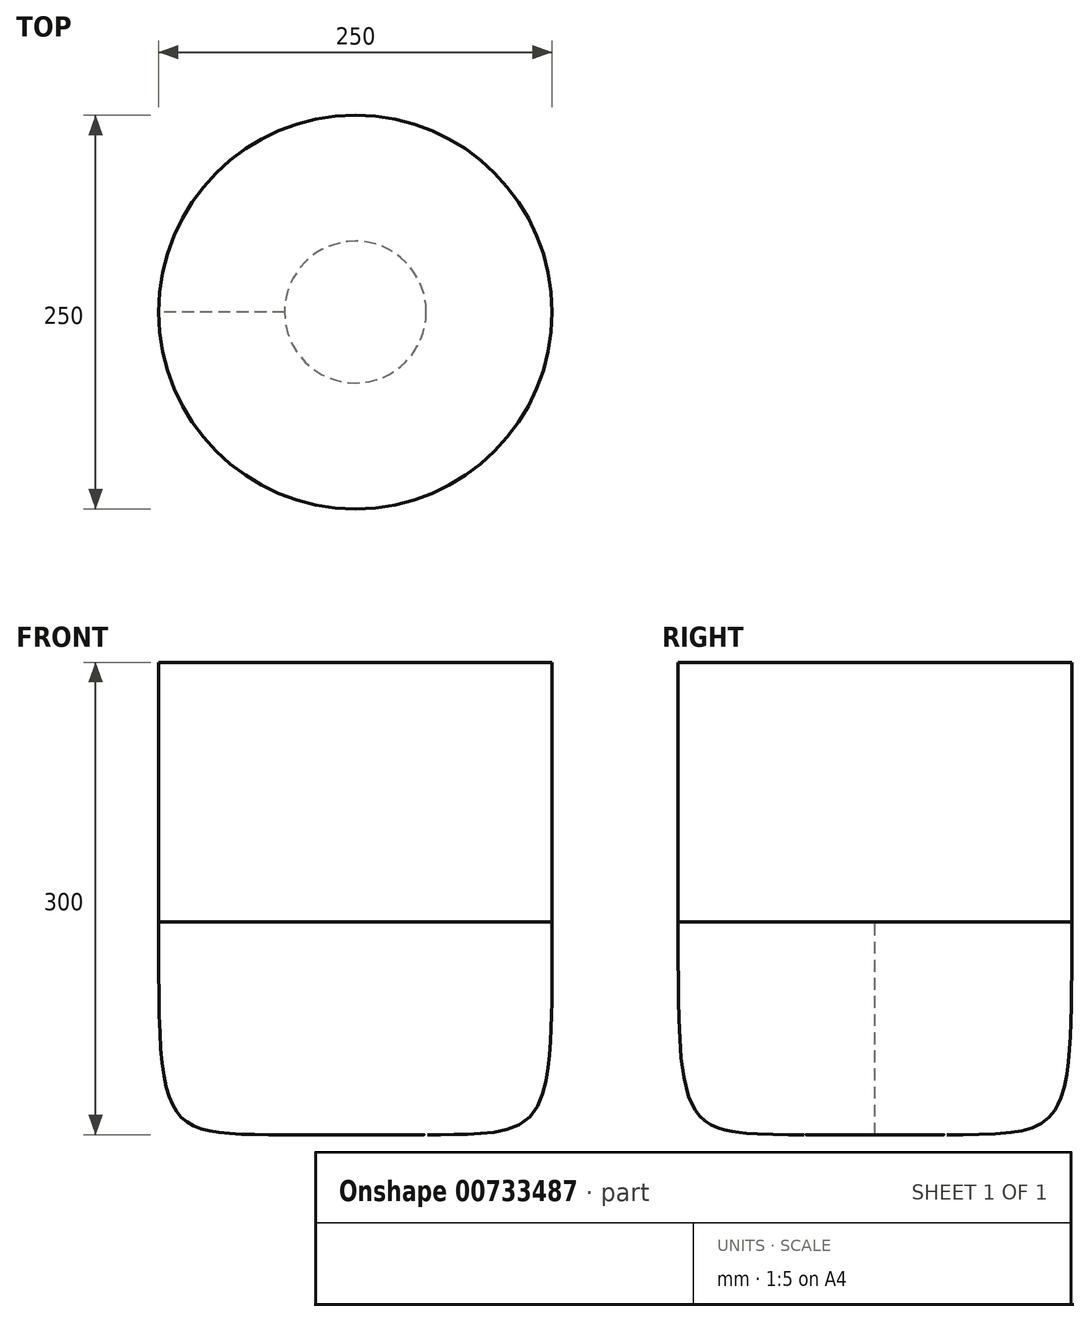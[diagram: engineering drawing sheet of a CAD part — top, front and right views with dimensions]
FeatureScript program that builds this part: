
annotation { "Feature Type Name" : "Feature", "Feature Type Description" : "" }
export const myFeature = defineFeature(function(context is Context, id is Id, definition is map)
    precondition{}
    {
        {
            var Q0;
            Q0=qCreatedBy(makeId("Front.planeOp"),FACE);
            var sketch = newSketch(context, id + "F0", { "sketchPlane" : qUnion([Q0])});
            skLineSegment(sketch, "E0.bottom", {"start": v(125, 150) * mm, "end": v(-125, 150) * mm});
            skLineSegment(sketch, "E0.top", {"start": v(125, -150) * mm, "end": v(-125, -150) * mm});
            skLineSegment(sketch, "E0.left", {"start": v(125, 150) * mm, "end": v(125, -150) * mm});
            skLineSegment(sketch, "E0.right", {"start": v(-125, 150) * mm, "end": v(-125, -150) * mm});
            skPoint(sketch, "E1", {"position": v(0, -150) * mm});
            skPoint(sketch, "E2", {"position": v(-125, 0) * mm});
            skPoint(sketch, "E3", {"position": v(125, 0) * mm});
            skPoint(sketch, "E4", {"position": v(45, -150) * mm});
            skPoint(sketch, "E5", {"position": v(-45, -150) * mm});
            skPoint(sketch, "E6", {"position": v(-125, -15) * mm});
            skPoint(sketch, "E7", {"position": v(-125, 15) * mm});
            skPoint(sketch, "E8", {"position": v(125, -15) * mm});
            skPoint(sketch, "E9", {"position": v(125, 15) * mm});
            skLineSegment(sketch, "E10", {"start": v(0, -150) * mm, "end": v(0, 150) * mm});
            skFitSpline(sketch, "E11", {"points": [v(-45, -150) * mm, v(-125, -15) * mm], "startDerivative": vector(-240, 0) * mm, "endDerivative": vector(0, 405) * mm});
            skFitSpline(sketch, "E12", {"points": [v(45, -150) * mm, v(125, -15) * mm], "startDerivative": vector(240, 0) * mm, "endDerivative": vector(0, 405) * mm});
            skLineSegment(sketch, "E13.bottom", {"start": v(-125, 15) * mm, "end": v(-125, 15) * mm});
            skLineSegment(sketch, "E13.top", {"start": v(-125, -15) * mm, "end": v(-125, -15) * mm});
            skLineSegment(sketch, "E13.left", {"start": v(-125, 15) * mm, "end": v(-125, -15) * mm});
            skLineSegment(sketch, "E13.right", {"start": v(-125, 15) * mm, "end": v(-125, -15) * mm});
            skLineSegment(sketch, "E14.bottom", {"start": v(-146.44, -15) * mm, "end": v(-125, -15) * mm});
            skLineSegment(sketch, "E14.top", {"start": v(-146.44, 15) * mm, "end": v(-125, 15) * mm});
            skLineSegment(sketch, "E14.left", {"start": v(-146.44, -15) * mm, "end": v(-146.44, 15) * mm});
            skLineSegment(sketch, "E14.right", {"start": v(-125, -15) * mm, "end": v(-125, 15) * mm});
            skSolve(sketch);
        }
        {
            var Q0;
            {var subQ0=sQuery(id+"F0.wireOp",EDGE,"E10");Q0=makeQuery(id+"F0.imprint","IMPRINT",FACE,{"disambiguationData":[TD([[makeQuery(id+"F0.imprint","IMPRINT",EDGE,{"derivedFrom":subQ0}),1.0]])]});}
            var Q1;
            Q1=sQuery(id+"F0.wireOp",EDGE,"E10");
            revolve(context, id + "F1", {"surfaceOperationType" : NewSurfaceOperationType.NEW, "entities" : qUnion([Q0]), "axis" : qUnion([Q1]), "revolveType" : RevolveType.FULL});
        }
    });
